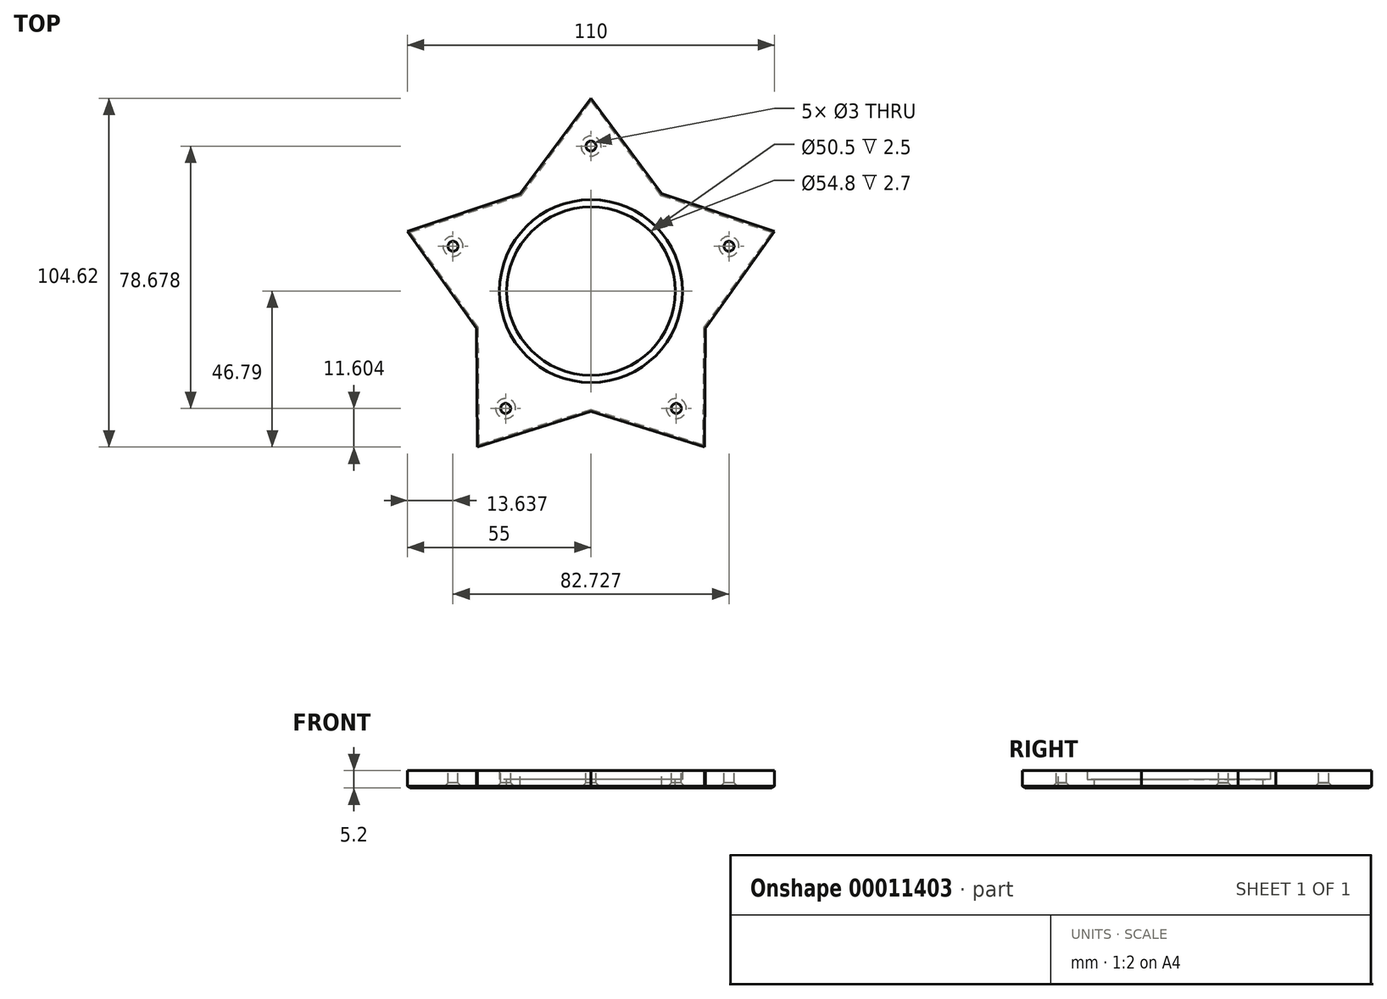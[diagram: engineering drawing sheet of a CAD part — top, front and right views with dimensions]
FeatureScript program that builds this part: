
annotation { "Feature Type Name" : "Feature", "Feature Type Description" : "" }
export const myFeature = defineFeature(function(context is Context, id is Id, definition is map)
    precondition{}
    {
        {
            var Q0;
            Q0=qCreatedBy(makeId("Top.planeOp"),FACE);
            var sketch = newSketch(context, id + "F0", { "sketchPlane" : qUnion([Q0])});
            skCircle(sketch, "E0", {"center": v(0, 0) * mm, "radius": 25.25 * mm});
            skCircle(sketch, "E1.cCircle", {"center": v(0, 0) * mm, "radius": 46.79 * mm, "construction": true});
            skLineSegment(sketch, "E1.0", {"start": v(0, 57.83) * mm, "end": v(55, 17.87) * mm, "construction": true});
            skLineSegment(sketch, "E1.1", {"start": v(55, 17.87) * mm, "end": v(34, -46.79) * mm, "construction": true});
            skLineSegment(sketch, "E1.2", {"start": v(34, -46.79) * mm, "end": v(-34, -46.79) * mm, "construction": true});
            skLineSegment(sketch, "E1.3", {"start": v(-34, -46.79) * mm, "end": v(-55, 17.87) * mm, "construction": true});
            skLineSegment(sketch, "E1.4", {"start": v(-55, 17.87) * mm, "end": v(0, 57.83) * mm, "construction": true});
            skPoint(sketch, "E1.0.midPoint", {"position": v(27.5, 37.85) * mm});
            skLineSegment(sketch, "E2", {"start": v(0, 57.83) * mm, "end": v(-21.18, 29.15) * mm});
            skLineSegment(sketch, "E3", {"start": v(-21.18, 29.15) * mm, "end": v(-55, 17.87) * mm});
            skLineSegment(sketch, "E4", {"start": v(-34.27, -11.14) * mm, "end": v(-34, -46.79) * mm});
            skLineSegment(sketch, "E5", {"start": v(-55, 17.87) * mm, "end": v(-34.27, -11.14) * mm});
            skLineSegment(sketch, "E6", {"start": v(-34, -46.79) * mm, "end": v(0, -36.04) * mm});
            skLineSegment(sketch, "E7", {"start": v(0, -36.04) * mm, "end": v(34, -46.79) * mm});
            skLineSegment(sketch, "E8", {"start": v(34, -46.79) * mm, "end": v(34.27, -11.14) * mm});
            skLineSegment(sketch, "E9", {"start": v(34.27, -11.14) * mm, "end": v(55, 17.87) * mm});
            skLineSegment(sketch, "E10", {"start": v(55, 17.87) * mm, "end": v(21.18, 29.15) * mm});
            skLineSegment(sketch, "E11", {"start": v(21.18, 29.15) * mm, "end": v(0, 57.83) * mm});
            skPoint(sketch, "E12", {"position": v(0, 43.5) * mm});
            skLineSegment(sketch, "E13", {"start": v(21.18, 29.15) * mm, "end": v(-21.18, 29.15) * mm, "construction": true});
            skLineSegment(sketch, "E14", {"start": v(0, 57.83) * mm, "end": v(0, 29.15) * mm, "construction": true});
            skPoint(sketch, "E15.1.0", {"position": v(-41.36, 13.44) * mm});
            skPoint(sketch, "E15.2.0", {"position": v(-25.56, -35.19) * mm});
            skPoint(sketch, "E15.3.0", {"position": v(25.56, -35.19) * mm});
            skPoint(sketch, "E15.4.0", {"position": v(41.36, 13.44) * mm});
            skSolve(sketch);
        }
        {
            var Q0;
            Q0 = qSketchRegion(id + "F0", true);
            extrude(context, id + "F1", {"entities" : qUnion([Q0]), "oppositeDirection" : true, "depth" : 2.5 * mm});
        }
        {
            var Q0;
            Q0=qCreatedBy(makeId("Top.planeOp"),FACE);
            var sketch = newSketch(context, id + "F2", { "sketchPlane" : qUnion([Q0])});
            skPoint(sketch, "E16.7", {"position": v(27.5, 37.85) * mm});
            skLineSegment(sketch, "E16.8", {"start": v(0, 57.83) * mm, "end": v(-21.18, 29.15) * mm});
            skLineSegment(sketch, "E16.9", {"start": v(-21.18, 29.15) * mm, "end": v(-55, 17.87) * mm});
            skLineSegment(sketch, "E16.10", {"start": v(-34.27, -11.14) * mm, "end": v(-34, -46.79) * mm});
            skLineSegment(sketch, "E16.11", {"start": v(-55, 17.87) * mm, "end": v(-34.27, -11.14) * mm});
            skLineSegment(sketch, "E16.12", {"start": v(-34, -46.79) * mm, "end": v(0, -36.04) * mm});
            skLineSegment(sketch, "E16.13", {"start": v(0, -36.04) * mm, "end": v(34, -46.79) * mm});
            skLineSegment(sketch, "E16.14", {"start": v(34, -46.79) * mm, "end": v(34.27, -11.14) * mm});
            skLineSegment(sketch, "E16.15", {"start": v(34.27, -11.14) * mm, "end": v(55, 17.87) * mm});
            skLineSegment(sketch, "E16.16", {"start": v(55, 17.87) * mm, "end": v(21.18, 29.15) * mm});
            skLineSegment(sketch, "E16.17", {"start": v(21.18, 29.15) * mm, "end": v(0, 57.83) * mm});
            skCircle(sketch, "E17", {"center": v(0, 0) * mm, "radius": 27.4 * mm});
            skSolve(sketch);
        }
        {
            var Q0;
            Q0 = qSketchRegion(id + "F2", true);
            extrude(context, id + "F3", {"entities" : qUnion([Q0]), "operationType" : NewBodyOperationType.ADD, "depth" : 2.7 * mm});
        }
        {
            var Q0;
            Q0=makeQuery(id+"F1.opExtrude","CAP_EDGE",EDGE,{"disambiguationData":[OSD([sQuery(id+"F0.wireOp",EDGE,"E4")])],"isStart":false});
            var Q1;
            Q1=makeQuery(id+"F1.opExtrude","CAP_EDGE",EDGE,{"disambiguationData":[OSD([sQuery(id+"F0.wireOp",EDGE,"E6")])],"isStart":false});
            var Q2;
            Q2=makeQuery(id+"F1.opExtrude","CAP_EDGE",EDGE,{"disambiguationData":[OSD([sQuery(id+"F0.wireOp",EDGE,"E7")])],"isStart":false});
            var Q3;
            Q3=makeQuery(id+"F1.opExtrude","CAP_EDGE",EDGE,{"disambiguationData":[OSD([sQuery(id+"F0.wireOp",EDGE,"E8")])],"isStart":false});
            var Q4;
            Q4=makeQuery(id+"F1.opExtrude","CAP_EDGE",EDGE,{"disambiguationData":[OSD([sQuery(id+"F0.wireOp",EDGE,"E9")])],"isStart":false});
            var Q5;
            Q5=makeQuery(id+"F1.opExtrude","CAP_EDGE",EDGE,{"disambiguationData":[OSD([sQuery(id+"F0.wireOp",EDGE,"E5")])],"isStart":false});
            var Q6;
            Q6=makeQuery(id+"F1.opExtrude","CAP_EDGE",EDGE,{"disambiguationData":[OSD([sQuery(id+"F0.wireOp",EDGE,"E3")])],"isStart":false});
            var Q7;
            Q7=makeQuery(id+"F1.opExtrude","CAP_EDGE",EDGE,{"disambiguationData":[OSD([sQuery(id+"F0.wireOp",EDGE,"E2")])],"isStart":false});
            var Q8;
            Q8=makeQuery(id+"F1.opExtrude","CAP_EDGE",EDGE,{"disambiguationData":[OSD([sQuery(id+"F0.wireOp",EDGE,"E11")])],"isStart":false});
            var Q9;
            Q9=makeQuery(id+"F1.opExtrude","CAP_EDGE",EDGE,{"disambiguationData":[OSD([sQuery(id+"F0.wireOp",EDGE,"E10")])],"isStart":false});
            chamfer(context, id + "F4", {"entities" : qUnion([Q0, Q1, Q2, Q3, Q4, Q5, Q6, Q7, Q8, Q9]), "width" : 0.5 * mm, "tangentPropagation" : true});
        }
        {
            var Q0;
            Q0=makeQuery(id+"F1.opExtrude","CAP_FACE",FACE,{"disambiguationData":[OSD([sQuery(id+"F0.wireOp",EDGE,"E0"),sQuery(id+"F0.wireOp",EDGE,"E2"),sQuery(id+"F0.wireOp",EDGE,"E3"),sQuery(id+"F0.wireOp",EDGE,"E4"),sQuery(id+"F0.wireOp",EDGE,"E5"),sQuery(id+"F0.wireOp",EDGE,"E6"),sQuery(id+"F0.wireOp",EDGE,"E7"),sQuery(id+"F0.wireOp",EDGE,"E8"),sQuery(id+"F0.wireOp",EDGE,"E9"),sQuery(id+"F0.wireOp",EDGE,"E10"),sQuery(id+"F0.wireOp",EDGE,"E11")])],"isStart":false});
            var sketch = newSketch(context, id + "F5", { "sketchPlane" : qUnion([Q0])});
            skPoint(sketch, "E18.1", {"position": v(0, -43.5) * mm});
            skPoint(sketch, "E19.0", {"position": v(41.36, -13.44) * mm});
            skPoint(sketch, "E19.1", {"position": v(-41.36, -13.44) * mm});
            skPoint(sketch, "E19.2", {"position": v(-25.56, 35.19) * mm});
            skPoint(sketch, "E19.3", {"position": v(25.56, 35.19) * mm});
            skSolve(sketch);
        }
        {
            var Q0;
            Q0=sQuery(id+"F5.wireOp",VERTEX,"E18.1");
            var Q1;
            Q1=sQuery(id+"F5.wireOp",VERTEX,"E19.0");
            var Q2;
            Q2=sQuery(id+"F5.wireOp",VERTEX,"E19.3");
            var Q3;
            Q3=sQuery(id+"F5.wireOp",VERTEX,"E19.2");
            var Q4;
            Q4=sQuery(id+"F5.wireOp",VERTEX,"E19.1");
            var Q5;
            Q5=makeQuery(id+"F1.opExtrude","SWEPT_BODY",BODY,{"disambiguationData":[OSD([sQuery(id+"F0.wireOp",EDGE,"E0"),sQuery(id+"F0.wireOp",EDGE,"E2"),sQuery(id+"F0.wireOp",EDGE,"E3"),sQuery(id+"F0.wireOp",EDGE,"E4"),sQuery(id+"F0.wireOp",EDGE,"E5"),sQuery(id+"F0.wireOp",EDGE,"E6"),sQuery(id+"F0.wireOp",EDGE,"E7"),sQuery(id+"F0.wireOp",EDGE,"E8"),sQuery(id+"F0.wireOp",EDGE,"E9"),sQuery(id+"F0.wireOp",EDGE,"E10"),sQuery(id+"F0.wireOp",EDGE,"E11")])]});
            hole(context, id + "F6", {"style" : HoleStyle.C_SINK, "holeDiameter" : 3 * mm, "cSinkDiameter" : 6 * mm, "endStyle" : HoleEndStyle.THROUGH, "locations" : qUnion([Q0, Q1, Q2, Q3, Q4]), "scope" : qUnion([Q5]), "cSinkAngle" : 90 * degree});
        }
    });
